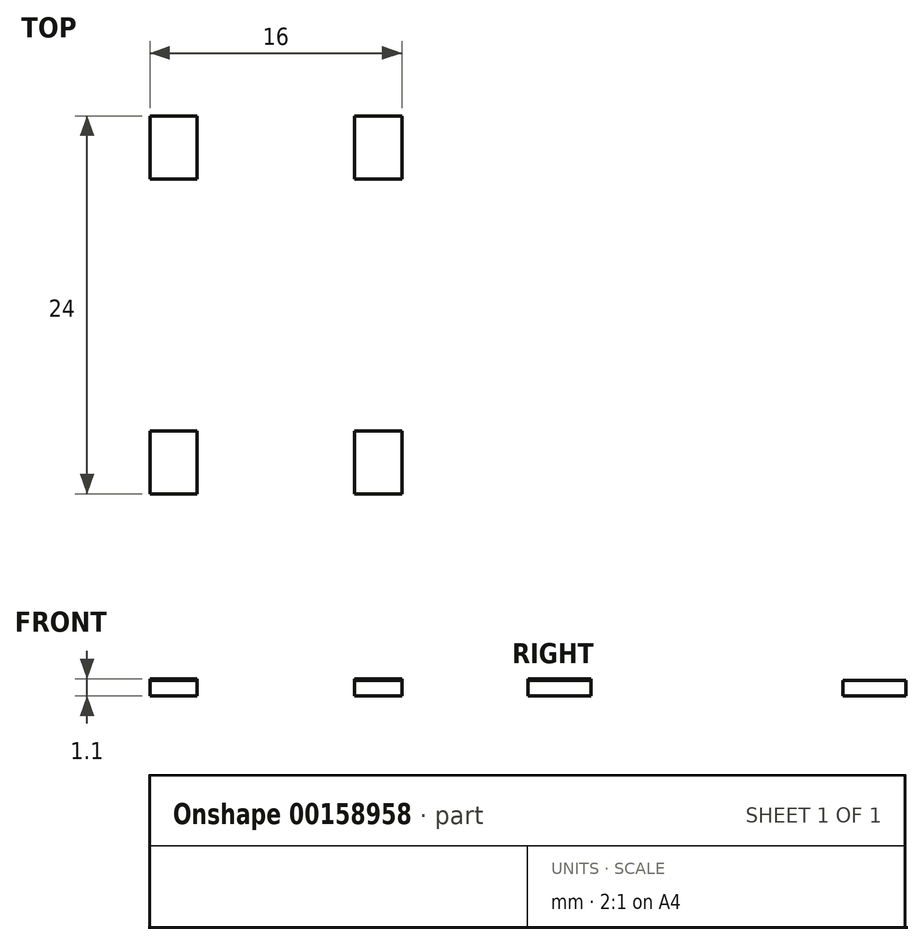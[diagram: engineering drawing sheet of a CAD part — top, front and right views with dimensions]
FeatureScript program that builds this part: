
annotation { "Feature Type Name" : "Feature", "Feature Type Description" : "" }
export const myFeature = defineFeature(function(context is Context, id is Id, definition is map)
    precondition{}
    {
        {
            var Q0;
            Q0=qCreatedBy(makeId("Top.planeOp"),FACE);
            var sketch = newSketch(context, id + "F0", { "sketchPlane" : qUnion([Q0])});
            skLineSegment(sketch, "E0.bottom", {"start": v(8, 12) * mm, "end": v(-8, 12) * mm});
            skLineSegment(sketch, "E0.top", {"start": v(8, -12) * mm, "end": v(-8, -12) * mm});
            skLineSegment(sketch, "E0.left", {"start": v(8, 12) * mm, "end": v(8, -12) * mm});
            skLineSegment(sketch, "E0.right", {"start": v(-8, 12) * mm, "end": v(-8, -12) * mm});
            skPoint(sketch, "E0.middle", {"position": v(0, 0) * mm});
            skLineSegment(sketch, "E1.bottom", {"start": v(-8, 12) * mm, "end": v(-5, 12) * mm});
            skLineSegment(sketch, "E1.top", {"start": v(-8, 8) * mm, "end": v(-5, 8) * mm});
            skLineSegment(sketch, "E1.left", {"start": v(-8, 12) * mm, "end": v(-8, 8) * mm});
            skLineSegment(sketch, "E1.right", {"start": v(-5, 12) * mm, "end": v(-5, 8) * mm});
            skLineSegment(sketch, "E2.MirrorCS", {"start": v(8, 12) * mm, "end": v(5, 12) * mm});
            skLineSegment(sketch, "E3.MirrorCS", {"start": v(8, 8) * mm, "end": v(5, 8) * mm});
            skLineSegment(sketch, "E4.MirrorCS", {"start": v(8, 12) * mm, "end": v(8, 8) * mm});
            skLineSegment(sketch, "E5.MirrorCS", {"start": v(5, 12) * mm, "end": v(5, 8) * mm});
            skLineSegment(sketch, "E6.MirrorCS", {"start": v(5, -12) * mm, "end": v(5, -8) * mm});
            skLineSegment(sketch, "E7.MirrorCS", {"start": v(8, -12) * mm, "end": v(8, -8) * mm});
            skLineSegment(sketch, "E8.MirrorCS", {"start": v(8, -8) * mm, "end": v(5, -8) * mm});
            skLineSegment(sketch, "E9.MirrorCS", {"start": v(8, -12) * mm, "end": v(5, -12) * mm});
            skLineSegment(sketch, "E10.MirrorCS", {"start": v(-5, -12) * mm, "end": v(-5, -8) * mm});
            skLineSegment(sketch, "E11.MirrorCS", {"start": v(-8, -12) * mm, "end": v(-8, -8) * mm});
            skLineSegment(sketch, "E12.MirrorCS", {"start": v(-8, -8) * mm, "end": v(-5, -8) * mm});
            skLineSegment(sketch, "E13.MirrorCS", {"start": v(-8, -12) * mm, "end": v(-5, -12) * mm});
            skLineSegment(sketch, "E14", {"start": v(0, 12) * mm, "end": v(0, -12) * mm, "construction": true});
            skSolve(sketch);
        }
        {
            var Q0;
            Q0=makeQuery(id+"F0.imprint","IMPRINT",FACE,{"disambiguationData":[TD([[makeQuery(id+"F0.imprint","IMPRINT",EDGE,{"derivedFrom":sQuery(id+"F0.wireOp",EDGE,"E0.bottom")}),1.0]])]});
            var Q1;
            Q1=makeQuery(id+"F0.imprint","IMPRINT",FACE,{"disambiguationData":[TD([[makeQuery(id+"F0.imprint","IMPRINT",EDGE,{"derivedFrom":sQuery(id+"F0.wireOp",EDGE,"E1.bottom")}),-1.0]])]});
            var Q2;
            Q2=makeQuery(id+"F0.imprint","IMPRINT",FACE,{"disambiguationData":[TD([[makeQuery(id+"F0.imprint","IMPRINT",EDGE,{"derivedFrom":sQuery(id+"F0.wireOp",EDGE,"E2.MirrorCS")}),1.0]])]});
            var Q3;
            {var subQ0=sQuery(id+"F0.wireOp",EDGE,"E6.MirrorCS");Q3=makeQuery(id+"F0.imprint","IMPRINT",FACE,{"disambiguationData":[TD([[makeQuery(id+"F0.imprint","IMPRINT",EDGE,{"derivedFrom":subQ0}),-1.0]])]});}
            var Q4;
            {var subQ0=sQuery(id+"F0.wireOp",EDGE,"E10.MirrorCS");Q4=makeQuery(id+"F0.imprint","IMPRINT",FACE,{"disambiguationData":[TD([[makeQuery(id+"F0.imprint","IMPRINT",EDGE,{"derivedFrom":subQ0}),1.0]])]});}
            extrude(context, id + "F1", {"entities" : qUnion([Q0, Q1, Q2, Q3, Q4]), "oppositeDirection" : true, "depth" : 1 * mm});
        }
        {
            var Q0;
            {var subQ0=sQuery(id+"F0.wireOp",EDGE,"E10.MirrorCS");Q0=makeQuery(id+"F0.imprint","IMPRINT",FACE,{"disambiguationData":[TD([[makeQuery(id+"F0.imprint","IMPRINT",EDGE,{"derivedFrom":subQ0}),1.0]])]});}
            var Q1;
            {var subQ0=sQuery(id+"F0.wireOp",EDGE,"E6.MirrorCS");Q1=makeQuery(id+"F0.imprint","IMPRINT",FACE,{"disambiguationData":[TD([[makeQuery(id+"F0.imprint","IMPRINT",EDGE,{"derivedFrom":subQ0}),-1.0]])]});}
            var Q2;
            Q2=makeQuery(id+"F0.imprint","IMPRINT",FACE,{"disambiguationData":[TD([[makeQuery(id+"F0.imprint","IMPRINT",EDGE,{"derivedFrom":sQuery(id+"F0.wireOp",EDGE,"E2.MirrorCS")}),1.0]])]});
            var Q3;
            Q3=makeQuery(id+"F0.imprint","IMPRINT",FACE,{"disambiguationData":[TD([[makeQuery(id+"F0.imprint","IMPRINT",EDGE,{"derivedFrom":sQuery(id+"F0.wireOp",EDGE,"E1.bottom")}),-1.0]])]});
            extrude(context, id + "F2", {"entities" : qUnion([Q0, Q1, Q2, Q3]), "depth" : 0.1 * mm});
        }
    });
